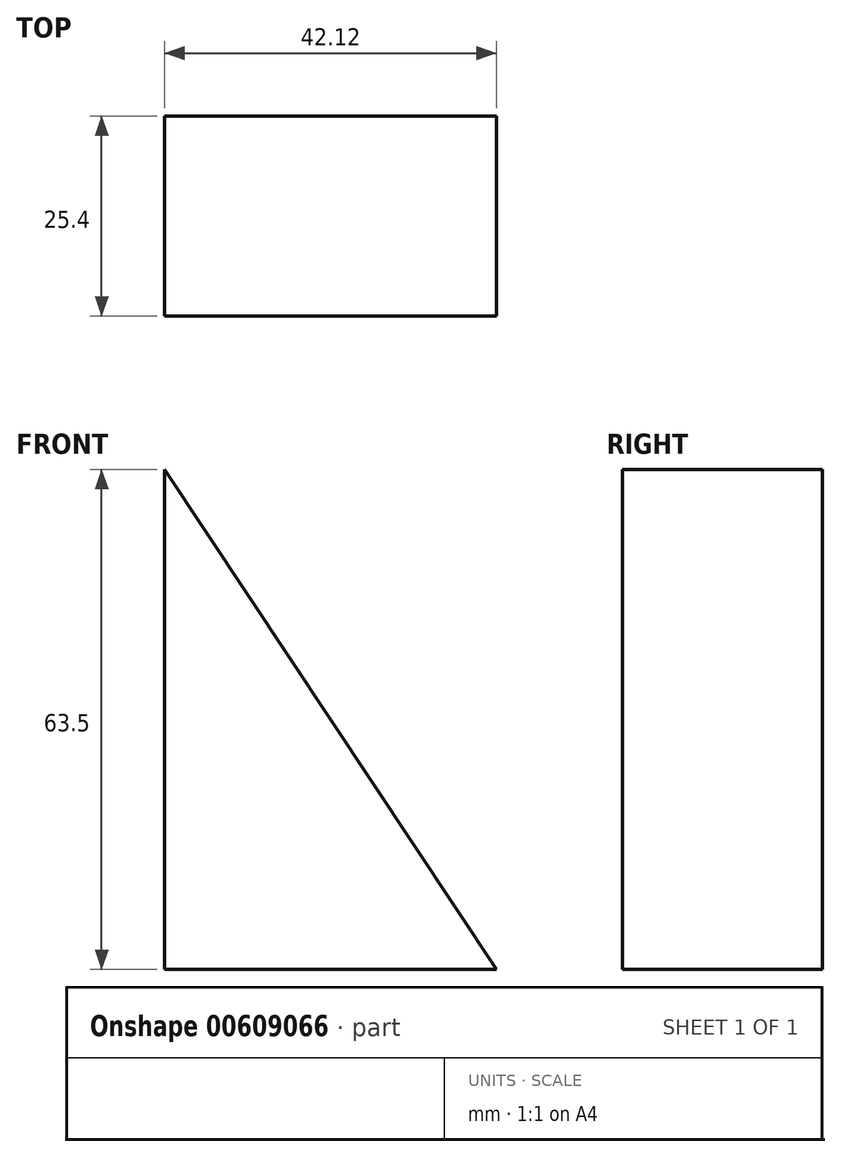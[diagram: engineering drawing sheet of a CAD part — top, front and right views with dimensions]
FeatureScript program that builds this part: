
annotation { "Feature Type Name" : "Feature", "Feature Type Description" : "" }
export const myFeature = defineFeature(function(context is Context, id is Id, definition is map)
    precondition{}
    {
        {
            var Q0;
            Q0=qCreatedBy(makeId("Front.planeOp"),FACE);
            var sketch = newSketch(context, id + "F0", { "sketchPlane" : qUnion([Q0])});
            skLineSegment(sketch, "E0", {"start": v(0, 0) * mm, "end": v(0, 63.5) * mm});
            skLineSegment(sketch, "E1", {"start": v(0, 63.5) * mm, "end": v(42.12, 0) * mm});
            skLineSegment(sketch, "E2", {"start": v(0, 0) * mm, "end": v(42.12, 0) * mm});
            skSolve(sketch);
        }
        {
            var Q0;
            Q0=makeQuery(id+"F0.imprint","IMPRINT",FACE,{"disambiguationData":[TD([[makeQuery(id+"F0.imprint","IMPRINT",EDGE,{"derivedFrom":sQuery(id+"F0.wireOp",EDGE,"E0")}),-1.0]])]});
            extrude(context, id + "F1", {"entities" : qUnion([Q0]), "depth" : 25.4 * mm, "offsetDistance" : 25.4 * mm});
        }
    });
